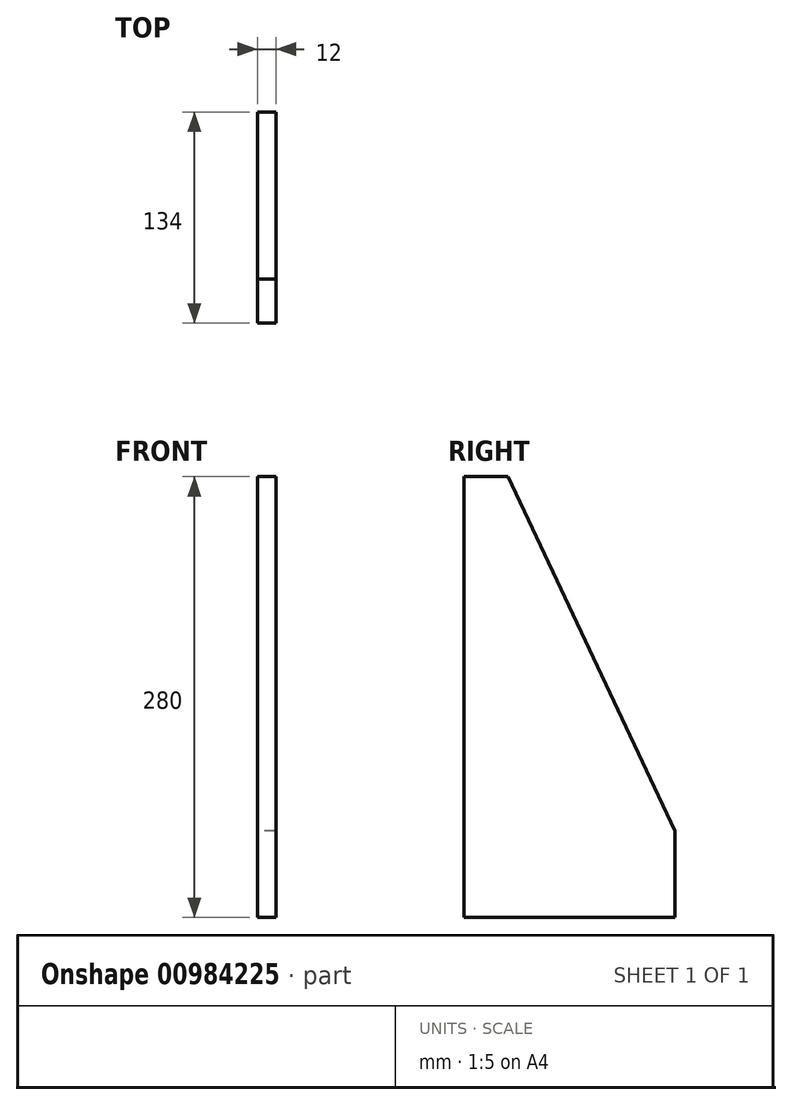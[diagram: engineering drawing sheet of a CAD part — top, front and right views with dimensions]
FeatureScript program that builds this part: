
annotation { "Feature Type Name" : "Feature", "Feature Type Description" : "" }
export const myFeature = defineFeature(function(context is Context, id is Id, definition is map)
    precondition{}
    {
        {
            var Q0;
            Q0=qCreatedBy(makeId("Right.planeOp"),FACE);
            var sketch = newSketch(context, id + "F0", { "sketchPlane" : qUnion([Q0])});
            skLineSegment(sketch, "E0", {"start": v(-51.02, -126.77) * mm, "end": v(-51.02, 153.23) * mm});
            skLineSegment(sketch, "E1", {"start": v(-51.02, 153.23) * mm, "end": v(-23.02, 153.23) * mm});
            skLineSegment(sketch, "E2", {"start": v(-23.02, 153.23) * mm, "end": v(82.98, -71.77) * mm});
            skLineSegment(sketch, "E3", {"start": v(82.98, -71.77) * mm, "end": v(82.98, -126.77) * mm});
            skLineSegment(sketch, "E4", {"start": v(82.98, -126.77) * mm, "end": v(-51.02, -126.77) * mm});
            skSolve(sketch);
        }
        {
            var Q0;
            Q0=makeQuery(id+"F0.imprint","IMPRINT",FACE,{"disambiguationData":[TD([[makeQuery(id+"F0.imprint","IMPRINT",EDGE,{"derivedFrom":sQuery(id+"F0.wireOp",EDGE,"E0")}),-1.0]])]});
            extrude(context, id + "F1", {"entities" : qUnion([Q0]), "depth" : 12 * mm, "offsetDistance" : 25 * mm});
        }
    });
